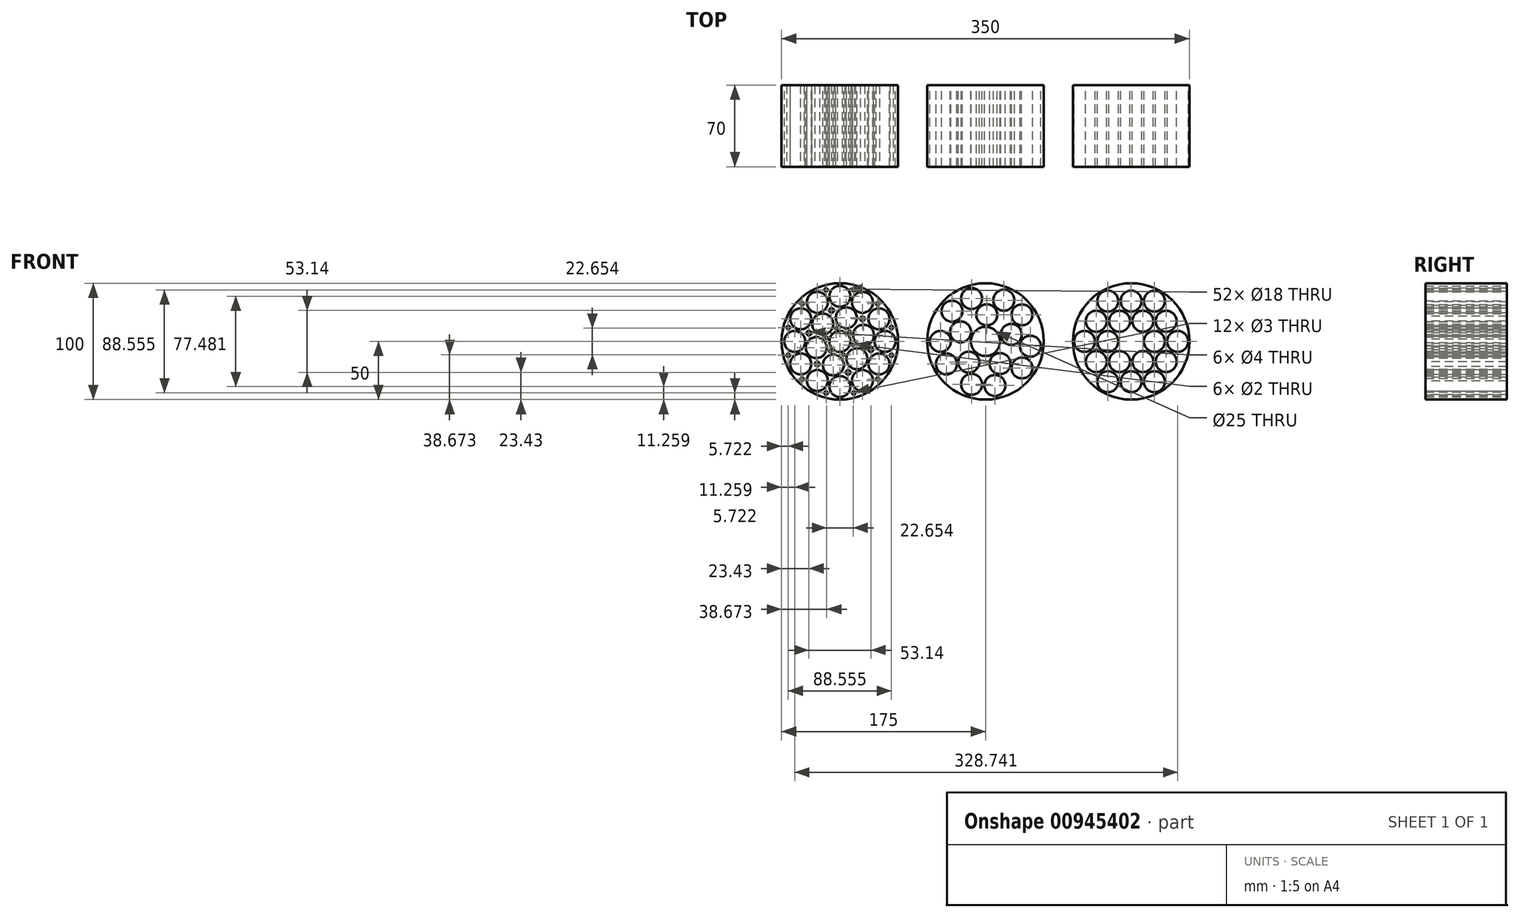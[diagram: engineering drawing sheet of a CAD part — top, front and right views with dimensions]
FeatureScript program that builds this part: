
annotation { "Feature Type Name" : "Feature", "Feature Type Description" : "" }
export const myFeature = defineFeature(function(context is Context, id is Id, definition is map)
    precondition{}
    {
        {
            var Q0;
            Q0=qCreatedBy(makeId("Front.planeOp"),FACE);
            var sketch = newSketch(context, id + "F0", { "sketchPlane" : qUnion([Q0])});
            skCircle(sketch, "E0", {"center": v(0, 0) * mm, "radius": 9 * mm});
            skCircle(sketch, "E1", {"center": v(-14.72, 14.92) * mm, "radius": 9 * mm});
            skCircle(sketch, "E2.1.0", {"center": v(-20.28, -5.29) * mm, "radius": 9 * mm});
            skCircle(sketch, "E2.2.0", {"center": v(-5.56, -20.2) * mm, "radius": 9 * mm});
            skCircle(sketch, "E2.3.0", {"center": v(14.72, -14.92) * mm, "radius": 9 * mm});
            skCircle(sketch, "E2.4.0", {"center": v(20.28, 5.29) * mm, "radius": 9 * mm});
            skCircle(sketch, "E2.5.0", {"center": v(5.56, 20.2) * mm, "radius": 9 * mm});
            skCircle(sketch, "E3", {"center": v(-38.74, 0) * mm, "radius": 9 * mm});
            skCircle(sketch, "E4.1.0", {"center": v(-33.55, -19.37) * mm, "radius": 9 * mm});
            skCircle(sketch, "E4.2.0", {"center": v(-19.37, -33.55) * mm, "radius": 9 * mm});
            skCircle(sketch, "E4.3.0", {"center": v(0, -38.74) * mm, "radius": 9 * mm});
            skCircle(sketch, "E4.4.0", {"center": v(19.37, -33.55) * mm, "radius": 9 * mm});
            skCircle(sketch, "E4.5.0", {"center": v(33.55, -19.37) * mm, "radius": 9 * mm});
            skCircle(sketch, "E4.6.0", {"center": v(38.74, 0) * mm, "radius": 9 * mm});
            skCircle(sketch, "E4.7.0", {"center": v(33.55, 19.37) * mm, "radius": 9 * mm});
            skCircle(sketch, "E5.1.8.0", {"center": v(19.37, 33.55) * mm, "radius": 9 * mm});
            skCircle(sketch, "E5.1.9.0", {"center": v(0, 38.74) * mm, "radius": 9 * mm});
            skCircle(sketch, "E5.1.10.0", {"center": v(-19.37, 33.55) * mm, "radius": 9 * mm});
            skCircle(sketch, "E5.1.11.0", {"center": v(-33.55, 19.37) * mm, "radius": 9 * mm});
            skCircle(sketch, "E6", {"center": v(0, 0) * mm, "radius": 50 * mm});
            skSolve(sketch);
        }
        {
            var Q0;
            Q0=qCreatedBy(makeId("Front.planeOp"),FACE);
            var sketch = newSketch(context, id + "F1", { "sketchPlane" : qUnion([Q0])});
            skCircle(sketch, "E7", {"center": v(-40, 0) * mm, "radius": 9 * mm});
            skCircle(sketch, "E8.1.0.0", {"center": v(-20, 0) * mm, "radius": 9 * mm});
            skCircle(sketch, "E8.2.0.0", {"center": v(0, 0) * mm, "radius": 9 * mm, "construction": true});
            skCircle(sketch, "E8.3.0.0", {"center": v(20, 0) * mm, "radius": 9 * mm});
            skLineSegment(sketch, "E8.direction1", {"start": v(-40, 0) * mm, "end": v(-20, 0) * mm, "construction": true});
            skCircle(sketch, "E9", {"center": v(-30, 17.32) * mm, "radius": 9 * mm});
            skCircle(sketch, "E10.1.0.0", {"center": v(-10, 17.32) * mm, "radius": 9 * mm});
            skCircle(sketch, "E10.2.0.0", {"center": v(10, 17.32) * mm, "radius": 9 * mm});
            skLineSegment(sketch, "E10.direction1", {"start": v(-30, 17.32) * mm, "end": v(-10, 17.32) * mm, "construction": true});
            skCircle(sketch, "E11", {"center": v(-20, 34.64) * mm, "radius": 9 * mm});
            skCircle(sketch, "E12.1.0.0", {"center": v(0, 34.64) * mm, "radius": 9 * mm});
            skLineSegment(sketch, "E12.direction1", {"start": v(-20, 34.64) * mm, "end": v(0, 34.64) * mm, "construction": true});
            skCircle(sketch, "E13", {"center": v(0, 0) * mm, "radius": 50 * mm});
            skCircle(sketch, "E14.0.4.0", {"center": v(40, 0) * mm, "radius": 9 * mm});
            skCircle(sketch, "E15.0.3.0", {"center": v(30, 17.32) * mm, "radius": 9 * mm});
            skCircle(sketch, "E16.0.2.0", {"center": v(20, 34.64) * mm, "radius": 9 * mm});
            skCircle(sketch, "E17.MirrorC", {"center": v(-10, -17.32) * mm, "radius": 9 * mm});
            skCircle(sketch, "E18.MirrorC", {"center": v(-20, -34.64) * mm, "radius": 9 * mm});
            skLineSegment(sketch, "E19.MirrorCS", {"start": v(-20, -34.64) * mm, "end": v(0, -34.64) * mm, "construction": true});
            skLineSegment(sketch, "E20.MirrorCS", {"start": v(-30, -17.32) * mm, "end": v(-10, -17.32) * mm, "construction": true});
            skCircle(sketch, "E21.MirrorC", {"center": v(20, -34.64) * mm, "radius": 9 * mm});
            skCircle(sketch, "E22.MirrorC", {"center": v(-30, -17.32) * mm, "radius": 9 * mm});
            skCircle(sketch, "E23.MirrorC", {"center": v(10, -17.32) * mm, "radius": 9 * mm});
            skCircle(sketch, "E24.MirrorC", {"center": v(30, -17.32) * mm, "radius": 9 * mm});
            skCircle(sketch, "E25.MirrorC", {"center": v(0, -34.64) * mm, "radius": 9 * mm});
            skSolve(sketch);
        }
        {
            var Q0;
            Q0=makeQuery(id+"F1.imprint","IMPRINT",FACE,{"disambiguationData":[TD([[makeQuery(id+"F1.imprint","IMPRINT",EDGE,{"derivedFrom":sQuery(id+"F1.wireOp",EDGE,"E7")}),-1.0]])]});
            extrude(context, id + "F2", {"entities" : qUnion([Q0]), "depth" : 70 * mm, "offsetDistance" : 25 * mm});
        }
        {
            var Q0;
            Q0=makeQuery(id+"F2.opExtrude","SWEPT_BODY",BODY,{"disambiguationData":[OSD([sQuery(id+"F1.wireOp",EDGE,"E7"),sQuery(id+"F1.wireOp",EDGE,"E8.1.0.0"),sQuery(id+"F1.wireOp",EDGE,"E8.3.0.0"),sQuery(id+"F1.wireOp",EDGE,"E9"),sQuery(id+"F1.wireOp",EDGE,"E10.1.0.0"),sQuery(id+"F1.wireOp",EDGE,"E10.2.0.0"),sQuery(id+"F1.wireOp",EDGE,"E11"),sQuery(id+"F1.wireOp",EDGE,"E12.1.0.0"),sQuery(id+"F1.wireOp",EDGE,"E13"),sQuery(id+"F1.wireOp",EDGE,"E14.0.4.0"),sQuery(id+"F1.wireOp",EDGE,"E15.0.3.0"),sQuery(id+"F1.wireOp",EDGE,"E16.0.2.0"),sQuery(id+"F1.wireOp",EDGE,"E17.MirrorC"),sQuery(id+"F1.wireOp",EDGE,"E18.MirrorC"),sQuery(id+"F1.wireOp",EDGE,"E21.MirrorC"),sQuery(id+"F1.wireOp",EDGE,"E22.MirrorC"),sQuery(id+"F1.wireOp",EDGE,"E23.MirrorC"),sQuery(id+"F1.wireOp",EDGE,"E24.MirrorC"),sQuery(id+"F1.wireOp",EDGE,"E25.MirrorC")])]});
            var Q1;
            Q1=sQuery(id+"F0.wireOp",VERTEX,"E0.center");
            var Q2;
            Q2=sQuery(id+"F0.wireOp",VERTEX,"E4.6.0.center");
            var Q3;
            Q3=qCreatedBy(makeId("Right.planeOp"),FACE);
            transform(context, id + "F3", {"entities" : qUnion([Q0]), "transformType" : TransformType.TRANSLATION_DISTANCE, "transformDirection" : qUnion([Q3]), "distance" : 125 * mm, "makeCopy" : false});
        }
        {
            var Q0;
            Q0 = qSketchRegion(id + "F0", true);
            extrude(context, id + "F4", {"entities" : qUnion([Q0]), "depth" : 70 * mm, "offsetDistance" : 25 * mm});
        }
        {
            var Q0;
            Q0=makeQuery(id+"F4.opExtrude","SWEPT_BODY",BODY,{"disambiguationData":[OSD([sQuery(id+"F0.wireOp",EDGE,"E0"),sQuery(id+"F0.wireOp",EDGE,"E1"),sQuery(id+"F0.wireOp",EDGE,"E2.1.0"),sQuery(id+"F0.wireOp",EDGE,"E2.2.0"),sQuery(id+"F0.wireOp",EDGE,"E2.3.0"),sQuery(id+"F0.wireOp",EDGE,"E2.4.0"),sQuery(id+"F0.wireOp",EDGE,"E2.5.0"),sQuery(id+"F0.wireOp",EDGE,"E3"),sQuery(id+"F0.wireOp",EDGE,"E4.1.0"),sQuery(id+"F0.wireOp",EDGE,"E4.2.0"),sQuery(id+"F0.wireOp",EDGE,"E4.3.0"),sQuery(id+"F0.wireOp",EDGE,"E4.4.0"),sQuery(id+"F0.wireOp",EDGE,"E4.5.0"),sQuery(id+"F0.wireOp",EDGE,"E4.6.0"),sQuery(id+"F0.wireOp",EDGE,"E4.7.0"),sQuery(id+"F0.wireOp",EDGE,"E5.1.8.0"),sQuery(id+"F0.wireOp",EDGE,"E5.1.9.0"),sQuery(id+"F0.wireOp",EDGE,"E5.1.10.0"),sQuery(id+"F0.wireOp",EDGE,"E5.1.11.0"),sQuery(id+"F0.wireOp",EDGE,"E6")])]});
            var Q1;
            Q1=qCreatedBy(makeId("Right.planeOp"),FACE);
            transform(context, id + "F5", {"entities" : qUnion([Q0]), "transformType" : TransformType.TRANSLATION_DISTANCE, "transformDirection" : qUnion([Q1]), "distance" : 125 * mm, "oppositeDirection" : true, "makeCopy" : false});
        }
        {
            var Q0;
            Q0=qCreatedBy(makeId("Front.planeOp"),FACE);
            var sketch = newSketch(context, id + "F6", { "sketchPlane" : qUnion([Q0])});
            skCircle(sketch, "E26", {"center": v(0, 0) * mm, "radius": 12.5 * mm});
            skCircle(sketch, "E27", {"center": v(-21.36, 8.13) * mm, "radius": 9 * mm});
            skCircle(sketch, "E28.1.0", {"center": v(-14.33, -17.8) * mm, "radius": 9 * mm});
            skCircle(sketch, "E28.2.0", {"center": v(12.5, -19.13) * mm, "radius": 9 * mm});
            skCircle(sketch, "E28.3.0", {"center": v(22.05, 5.98) * mm, "radius": 9 * mm});
            skCircle(sketch, "E28.4.0", {"center": v(1.13, 22.82) * mm, "radius": 9 * mm});
            skCircle(sketch, "E29", {"center": v(-38.74, 0) * mm, "radius": 9 * mm});
            skCircle(sketch, "E30", {"center": v(0, 0) * mm, "radius": 50 * mm});
            skCircle(sketch, "E31.1.0", {"center": v(-28.79, 25.92) * mm, "radius": 9 * mm});
            skLineSegment(sketch, "E31.anchor1", {"start": v(0, 0) * mm, "end": v(-38.74, 0) * mm, "construction": true});
            skLineSegment(sketch, "E31.anchor2", {"start": v(0, 0) * mm, "end": v(-28.79, 25.92) * mm, "construction": true});
            skCircle(sketch, "E32.1.0", {"center": v(-11.97, -36.84) * mm, "radius": 9 * mm});
            skCircle(sketch, "E32.1.1", {"center": v(-33.55, -19.37) * mm, "radius": 9 * mm});
            skCircle(sketch, "E32.2.0", {"center": v(31.34, -22.77) * mm, "radius": 9 * mm});
            skCircle(sketch, "E32.2.1", {"center": v(8.05, -37.9) * mm, "radius": 9 * mm});
            skCircle(sketch, "E32.3.0", {"center": v(31.34, 22.77) * mm, "radius": 9 * mm});
            skCircle(sketch, "E32.3.1", {"center": v(38.53, -4.05) * mm, "radius": 9 * mm});
            skCircle(sketch, "E32.4.0", {"center": v(-11.97, 36.84) * mm, "radius": 9 * mm});
            skCircle(sketch, "E32.4.1", {"center": v(15.76, 35.4) * mm, "radius": 9 * mm});
            skSolve(sketch);
        }
        {
            var Q0;
            Q0=makeQuery(id+"F6.imprint","IMPRINT",FACE,{"disambiguationData":[TD([[makeQuery(id+"F6.imprint","IMPRINT",EDGE,{"derivedFrom":sQuery(id+"F6.wireOp",EDGE,"E26")}),-1.0]])]});
            extrude(context, id + "F7", {"entities" : qUnion([Q0]), "depth" : 70 * mm, "offsetDistance" : 25 * mm});
        }
        {
            var Q0;
            Q0=makeQuery(id+"F4.opExtrude","CAP_FACE",FACE,{"disambiguationData":[OSD([sQuery(id+"F0.wireOp",EDGE,"E0"),sQuery(id+"F0.wireOp",EDGE,"E1"),sQuery(id+"F0.wireOp",EDGE,"E2.1.0"),sQuery(id+"F0.wireOp",EDGE,"E2.2.0"),sQuery(id+"F0.wireOp",EDGE,"E2.3.0"),sQuery(id+"F0.wireOp",EDGE,"E2.4.0"),sQuery(id+"F0.wireOp",EDGE,"E2.5.0"),sQuery(id+"F0.wireOp",EDGE,"E3"),sQuery(id+"F0.wireOp",EDGE,"E4.1.0"),sQuery(id+"F0.wireOp",EDGE,"E4.2.0"),sQuery(id+"F0.wireOp",EDGE,"E4.3.0"),sQuery(id+"F0.wireOp",EDGE,"E4.4.0"),sQuery(id+"F0.wireOp",EDGE,"E4.5.0"),sQuery(id+"F0.wireOp",EDGE,"E4.6.0"),sQuery(id+"F0.wireOp",EDGE,"E4.7.0"),sQuery(id+"F0.wireOp",EDGE,"E5.1.8.0"),sQuery(id+"F0.wireOp",EDGE,"E5.1.9.0"),sQuery(id+"F0.wireOp",EDGE,"E5.1.10.0"),sQuery(id+"F0.wireOp",EDGE,"E5.1.11.0"),sQuery(id+"F0.wireOp",EDGE,"E6")])],"isStart":false});
            var sketch = newSketch(context, id + "F8", { "sketchPlane" : qUnion([Q0])});
            skText(sketch, "E33", { "text": "18 holes / \n18mm", "fontName": "OpenSans-Regular.ttf"});
            skText(sketch, "E34", { "text": "15 holes/ 25 mm\n", "fontName": "OpenSans-Regular.ttf"});
            skText(sketch, "E35", { "text": "18 holes / 18 mm", "fontName": "OpenSans-Regular.ttf"});
            const initialGuessF8  = {"E33": [-0.14687, 0.0668, 1, 0, 0.006], "E34": [-0.03946, 0.04672, 1, 0, 0.00667], "E35": [0.07482, 0.04977, 1, 0, 0.00814]};
            skSetInitialGuess(sketch, initialGuessF8);
            skSolve(sketch);
        }
        {
            var Q0;
            Q0=makeQuery(id+"F8.imprint","IMPRINT",FACE,{"disambiguationData":[TD([[makeQuery(id+"F8.imprint","IMPRINT",EDGE,{"derivedFrom":makeQuery(id+"F4.opExtrude","CAP_EDGE",EDGE,{"disambiguationData":[OSD([sQuery(id+"F0.wireOp",EDGE,"E0")])],"isStart":false})}),-1.0]])]});
            var sketch = newSketch(context, id + "F9", { "sketchPlane" : qUnion([Q0])});
            skCircle(sketch, "E36", {"center": v(-151.57, 7.12) * mm, "radius": 2 * mm});
            skCircle(sketch, "E37.1.0", {"center": v(-144.45, -19.45) * mm, "radius": 2 * mm});
            skCircle(sketch, "E37.2.0", {"center": v(-117.88, -26.57) * mm, "radius": 2 * mm});
            skCircle(sketch, "E37.3.0", {"center": v(-98.43, -7.12) * mm, "radius": 2 * mm});
            skCircle(sketch, "E37.4.0", {"center": v(-105.55, 19.45) * mm, "radius": 2 * mm});
            skCircle(sketch, "E37.5.0", {"center": v(-132.12, 26.57) * mm, "radius": 2 * mm});
            skPoint(sketch, "E37.center", {"position": v(-125, 0) * mm});
            skCircle(sketch, "E38", {"center": v(-169.28, 11.86) * mm, "radius": 1.5 * mm});
            skCircle(sketch, "E39.1.0", {"center": v(-169.28, -11.86) * mm, "radius": 1.5 * mm});
            skCircle(sketch, "E39.2.0", {"center": v(-157.41, -32.41) * mm, "radius": 1.5 * mm});
            skCircle(sketch, "E40.1.3.0", {"center": v(-136.86, -44.28) * mm, "radius": 1.5 * mm});
            skCircle(sketch, "E40.1.4.0", {"center": v(-113.14, -44.28) * mm, "radius": 1.5 * mm});
            skCircle(sketch, "E40.1.5.0", {"center": v(-92.59, -32.41) * mm, "radius": 1.5 * mm});
            skCircle(sketch, "E41.1.6.0", {"center": v(-80.72, -11.86) * mm, "radius": 1.5 * mm});
            skCircle(sketch, "E41.1.7.0", {"center": v(-80.72, 11.86) * mm, "radius": 1.5 * mm});
            skCircle(sketch, "E41.1.8.0", {"center": v(-92.59, 32.41) * mm, "radius": 1.5 * mm});
            skCircle(sketch, "E41.1.9.0", {"center": v(-113.14, 44.28) * mm, "radius": 1.5 * mm});
            skCircle(sketch, "E41.1.10.0", {"center": v(-136.86, 44.28) * mm, "radius": 1.5 * mm});
            skCircle(sketch, "E41.1.11.0", {"center": v(-157.41, 32.41) * mm, "radius": 1.5 * mm});
            skCircle(sketch, "E42.0", {"center": v(-158.55, 19.37) * mm, "radius": 9 * mm, "construction": true});
            skCircle(sketch, "E43.0", {"center": v(-139.72, 14.92) * mm, "radius": 9 * mm, "construction": true});
            skCircle(sketch, "E44.0", {"center": v(-163.74, 0) * mm, "radius": 9 * mm, "construction": true});
            skCircle(sketch, "E45.0", {"center": v(-145.28, -5.29) * mm, "radius": 9 * mm, "construction": true});
            skLineSegment(sketch, "E46", {"start": v(-158.55, 19.37) * mm, "end": v(-163.74, 0) * mm, "construction": true});
            skLineSegment(sketch, "E47", {"start": v(-125, 0) * mm, "end": v(-183.67, 15.72) * mm, "construction": true});
            skCircle(sketch, "E48", {"center": v(-136.33, 3.04) * mm, "radius": 1 * mm});
            skCircle(sketch, "E49.1.0", {"center": v(-133.3, -8.3) * mm, "radius": 1 * mm});
            skCircle(sketch, "E49.2.0", {"center": v(-121.96, -11.33) * mm, "radius": 1 * mm});
            skCircle(sketch, "E49.3.0", {"center": v(-113.67, -3.04) * mm, "radius": 1 * mm});
            skCircle(sketch, "E49.4.0", {"center": v(-116.7, 8.3) * mm, "radius": 1 * mm});
            skCircle(sketch, "E49.5.0", {"center": v(-128.04, 11.33) * mm, "radius": 1 * mm});
            skSolve(sketch);
        }
        {
            var Q0;
            Q0 = qSketchRegion(id + "F9", true);
            extrude(context, id + "F10", {"entities" : qUnion([Q0]), "operationType" : NewBodyOperationType.REMOVE, "endBound" : BoundingType.THROUGH_ALL, "oppositeDirection" : true, "depth" : 25 * mm, "offsetDistance" : 25 * mm});
        }
        {
            var Q0;
            Q0=makeQuery(id+"F8.imprint","IMPRINT",FACE,{"disambiguationData":[TD([[makeQuery(id+"F8.imprint","IMPRINT",EDGE,{"derivedFrom":makeQuery(id+"F4.opExtrude","CAP_EDGE",EDGE,{"disambiguationData":[OSD([sQuery(id+"F0.wireOp",EDGE,"E0")])],"isStart":false})}),-1.0]])]});
            var sketch = newSketch(context, id + "F11", { "sketchPlane" : qUnion([Q0])});
            skCircle(sketch, "E50.0", {"center": v(-136.86, 44.28) * mm, "radius": 1.5 * mm});
            skCircle(sketch, "E50.1", {"center": v(-157.41, 32.41) * mm, "radius": 1.5 * mm});
            skCircle(sketch, "E50.2", {"center": v(-132.12, 26.57) * mm, "radius": 2 * mm});
            skCircle(sketch, "E50.3", {"center": v(-113.14, 44.28) * mm, "radius": 1.5 * mm});
            skCircle(sketch, "E50.4", {"center": v(-92.59, 32.41) * mm, "radius": 1.5 * mm});
            skCircle(sketch, "E50.5", {"center": v(-105.55, 19.45) * mm, "radius": 2 * mm});
            skCircle(sketch, "E50.6", {"center": v(-80.72, 11.86) * mm, "radius": 1.5 * mm});
            skCircle(sketch, "E50.7", {"center": v(-80.72, -11.86) * mm, "radius": 1.5 * mm});
            skCircle(sketch, "E50.8", {"center": v(-98.43, -7.12) * mm, "radius": 2 * mm});
            skCircle(sketch, "E50.9", {"center": v(-113.67, -3.04) * mm, "radius": 1 * mm});
            skCircle(sketch, "E50.10", {"center": v(-116.7, 8.3) * mm, "radius": 1 * mm});
            skCircle(sketch, "E50.11", {"center": v(-128.04, 11.33) * mm, "radius": 1 * mm});
            skCircle(sketch, "E50.12", {"center": v(-169.28, 11.86) * mm, "radius": 1.5 * mm});
            skCircle(sketch, "E50.13", {"center": v(-151.57, 7.12) * mm, "radius": 2 * mm});
            skCircle(sketch, "E50.14", {"center": v(-136.33, 3.04) * mm, "radius": 1 * mm});
            skCircle(sketch, "E50.15", {"center": v(-133.3, -8.3) * mm, "radius": 1 * mm});
            skCircle(sketch, "E50.16", {"center": v(-121.96, -11.33) * mm, "radius": 1 * mm});
            skCircle(sketch, "E50.17", {"center": v(-169.28, -11.86) * mm, "radius": 1.5 * mm});
            skCircle(sketch, "E50.18", {"center": v(-144.45, -19.45) * mm, "radius": 2 * mm});
            skCircle(sketch, "E50.19", {"center": v(-117.88, -26.57) * mm, "radius": 2 * mm});
            skCircle(sketch, "E50.20.0", {"center": v(-125, 0) * mm, "radius": 50 * mm});
            skCircle(sketch, "E50.21", {"center": v(-92.59, -32.41) * mm, "radius": 1.5 * mm});
            skCircle(sketch, "E50.22", {"center": v(-113.14, -44.28) * mm, "radius": 1.5 * mm});
            skCircle(sketch, "E50.23", {"center": v(-136.86, -44.28) * mm, "radius": 1.5 * mm});
            skCircle(sketch, "E50.24", {"center": v(-157.41, -32.41) * mm, "radius": 1.5 * mm});
            skCircle(sketch, "E51.0.0", {"center": v(-163.74, 0) * mm, "radius": 9 * mm});
            skSolve(sketch);
        }
        {
            var Q0;
            Q0 = qSketchRegion(id + "F11", true);
            var Q1;
            Q1=sQuery(id+"F11.wireOp",EDGE,"E50.20.0");
            extrude(context, id + "F12", {"entities" : qUnion([Q0]), "bodyType" : ToolBodyType.SURFACE, "surfaceEntities" : qUnion([Q1]), "depth" : 25 * mm, "offsetDistance" : 25 * mm});
        }
    });
